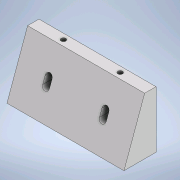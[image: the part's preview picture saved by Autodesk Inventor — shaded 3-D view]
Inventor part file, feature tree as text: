
AUTODESK INVENTOR PART (.ipt)
format: ipt  version: 2020.1 (Build 241239000, 239)  size: 191,488 bytes
history: native  units: mm
features: sketch x8, extrude x6, hole x2
ambient origin geometry x8: Origin, YZ Plane, XZ Plane, XY Plane, X Axis, Y Axis, Z Axis, Center Point
bodies: Volumenkörper1 (feature_tree)
feature tree (16):
  extrude  "Extrusion1"  Depth=20.0mm
  hole  "Bohrung1"  [1 undecoded]
  extrude  "Extrusion2"  TaperAngle=90.0deg  [1 undecoded]
  extrude  "Extrusion3"  Depth=50.0mm
  extrude  "Extrusion4"  Depth=10.0mm
  extrude  "Extrusion5"  Depth=50.0mm
  extrude  "Extrusion6"  Depth=206.0mm TaperAngle=0.0deg
  hole  "Bohrung2"  [1 undecoded]
  sketch  "Skizze1"  dims[d0=206.0mm d1=20.0mm]
  sketch  "Skizze2"  dims[d2=100.0mm d3=0.0mm d4=10.0mm]
  sketch  "Skizze3"  dims[d5=206.0mm d6=90.0deg]
  sketch  "Skizze4"  dims[d7=103.0mm d8=50.0mm]
  sketch  "Skizze5"  dims[d9=100.0mm]
  sketch  "Skizze6"  dims[d10=8.376mm d11=20.0mm d12=9.0mm d13=10.0mm d14=90.0deg d15=27.3mm d16=20.594885mm d17=120.0mm]
  sketch  "Skizze7"  dims[d18=19.198622mm d19=50.0mm]
  sketch  "Skizze8"  dims[d20=180.0deg d21=206.0mm d22=0.0mm d23=103.0mm d24=180.0deg d25=50.0mm d26=100.0mm d27=0.0mm d28=50.0mm d29=90.0deg d30=50.0mm d31=90.0deg d32=6.0mm d33=6.0mm d34=180.0deg d35=100.0mm d36=90.0deg d37=100.0mm d38=0.0mm d39=35.0mm d40=20.0mm d41=30.0mm d42=0.0mm d43=35.0mm d44=40.0mm d45=0.0mm d46=1.0mm d47=90.0deg d48=10.0mm d49=90.0deg d50=20.0mm d51=0.0mm d52=40.0mm d53=0.0mm d54=8.376mm d55=20.0mm d56=4.0mm d57=2.0mm d58=90.0deg d59=27.3mm d60=20.594885mm]
note: 3 required parameter values undecoded (feature->parameter linkage not recoverable at this tier; creation-order binding heuristic only, values carry confidence <= 0.55)
